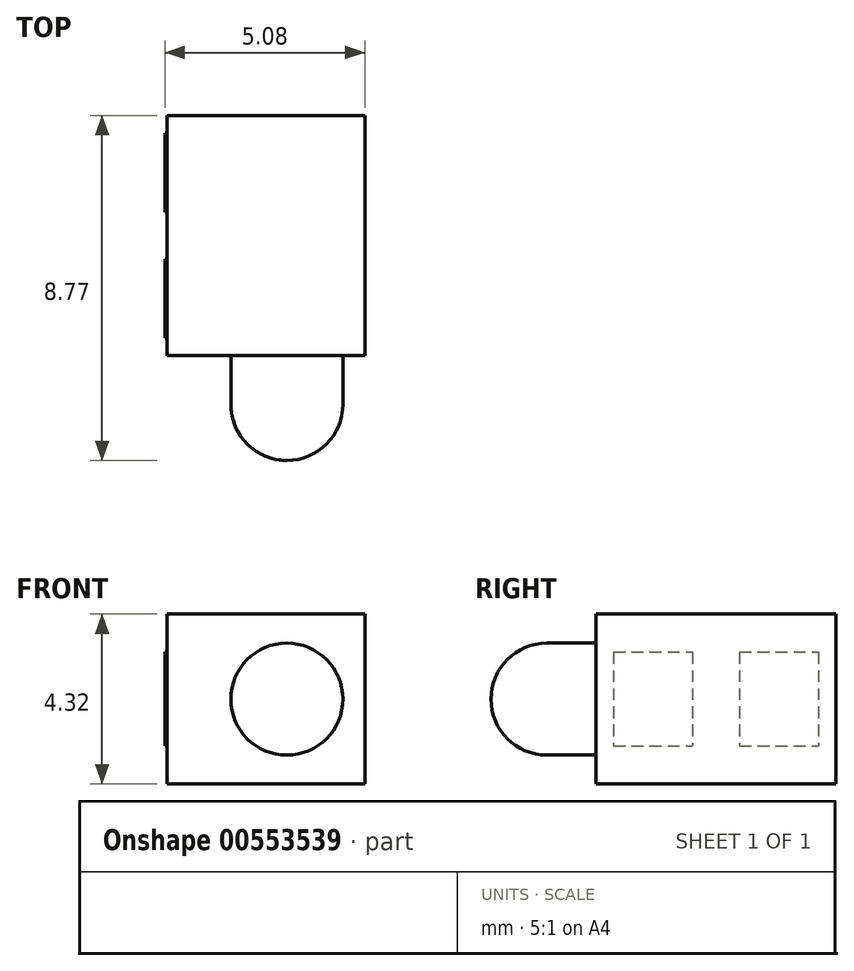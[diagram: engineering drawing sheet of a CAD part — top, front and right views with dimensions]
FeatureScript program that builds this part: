
annotation { "Feature Type Name" : "Feature", "Feature Type Description" : "" }
export const myFeature = defineFeature(function(context is Context, id is Id, definition is map)
    precondition{}
    {
        {
            var Q0;
            Q0=qCreatedBy(makeId("Top.planeOp"),FACE);
            cPlane(context, id + "F0", {"entities" : qUnion([Q0]), "cplaneType" : CPlaneType.OFFSET, "offset" : 2.16 * mm, "width" : 152.4 * mm, "height" : 152.4 * mm});
        }
        {
            var Q0;
            Q0=qCreatedBy(makeId("Top.planeOp"),FACE);
            var sketch = newSketch(context, id + "F1", { "sketchPlane" : qUnion([Q0])});
            skLineSegment(sketch, "E0.bottom", {"start": v(0, 0) * mm, "end": v(5.03, 0) * mm});
            skLineSegment(sketch, "E0.top", {"start": v(0, 6.1) * mm, "end": v(5.03, 6.1) * mm});
            skLineSegment(sketch, "E0.left", {"start": v(0, 0) * mm, "end": v(0, 6.1) * mm});
            skLineSegment(sketch, "E0.right", {"start": v(5.03, 0) * mm, "end": v(5.03, 6.1) * mm});
            skSolve(sketch);
        }
        {
            var Q0;
            Q0 = qSketchRegion(id + "F1", true);
            extrude(context, id + "F2", {"entities" : qUnion([Q0]), "depth" : 4.32 * mm, "offsetDistance" : 25.4 * mm});
        }
        {
            var Q0;
            Q0=qCreatedBy(id+"F0.planeOp",FACE);
            var sketch = newSketch(context, id + "F3", { "sketchPlane" : qUnion([Q0])});
            skLineSegment(sketch, "E1", {"start": v(3.05, 0) * mm, "end": v(1.63, 0) * mm});
            skLineSegment(sketch, "E2", {"start": v(1.63, 0) * mm, "end": v(1.63, -1.24) * mm});
            skArc(sketch, "E3", {"start": v(1.63, -1.24) * mm, "mid": v(2.04, -2.25) * mm, "end": v(3.05, -2.67) * mm});
            skLineSegment(sketch, "E4", {"start": v(3.05, -2.67) * mm, "end": v(3.05, 0) * mm});
            skLineSegment(sketch, "E5", {"start": v(3.05, -2.67) * mm, "end": v(3.05, -6.87) * mm, "construction": true});
            skSolve(sketch);
        }
        {
            var Q0;
            Q0 = qSketchRegion(id + "F3", true);
            var Q1;
            Q1=sQuery(id+"F3.wireOp",EDGE,"E5");
            revolve(context, id + "F4", {"entities" : qUnion([Q0]), "axis" : qUnion([Q1]), "revolveType" : RevolveType.FULL});
        }
        {
            var Q0;
            Q0=makeQuery(id+"F2.opExtrude","SWEPT_FACE",FACE,{"disambiguationData":[OSD([sQuery(id+"F1.wireOp",EDGE,"E0.left")])]});
            var sketch = newSketch(context, id + "F5", { "sketchPlane" : qUnion([Q0])});
            skLineSegment(sketch, "E6.bottom", {"start": v(-0.44, 3.35) * mm, "end": v(-2.45, 3.35) * mm});
            skLineSegment(sketch, "E6.top", {"start": v(-0.44, 0.97) * mm, "end": v(-2.45, 0.97) * mm});
            skLineSegment(sketch, "E6.left", {"start": v(-0.44, 3.35) * mm, "end": v(-0.44, 0.97) * mm});
            skLineSegment(sketch, "E6.right", {"start": v(-2.45, 3.35) * mm, "end": v(-2.45, 0.97) * mm});
            skLineSegment(sketch, "E7.bottom", {"start": v(-3.64, 3.35) * mm, "end": v(-5.65, 3.35) * mm});
            skLineSegment(sketch, "E7.top", {"start": v(-3.64, 0.97) * mm, "end": v(-5.65, 0.97) * mm});
            skLineSegment(sketch, "E7.left", {"start": v(-3.64, 3.35) * mm, "end": v(-3.64, 0.97) * mm});
            skLineSegment(sketch, "E7.right", {"start": v(-5.65, 3.35) * mm, "end": v(-5.65, 0.97) * mm});
            skLineSegment(sketch, "E8", {"start": v(-5.65, 3.35) * mm, "end": v(-6.1, 3.35) * mm, "construction": true});
            skLineSegment(sketch, "E9", {"start": v(-5.65, 3.35) * mm, "end": v(-5.65, 4.32) * mm, "construction": true});
            skLineSegment(sketch, "E10", {"start": v(-0.44, 0.97) * mm, "end": v(0, 0.97) * mm, "construction": true});
            skLineSegment(sketch, "E11", {"start": v(-0.44, 0.97) * mm, "end": v(-0.44, 0) * mm, "construction": true});
            skSolve(sketch);
        }
        {
            var Q0;
            Q0 = qSketchRegion(id + "F5", true);
            extrude(context, id + "F6", {"entities" : qUnion([Q0]), "depth" : 0.05 * mm, "offsetDistance" : 25.4 * mm});
        }
    });
